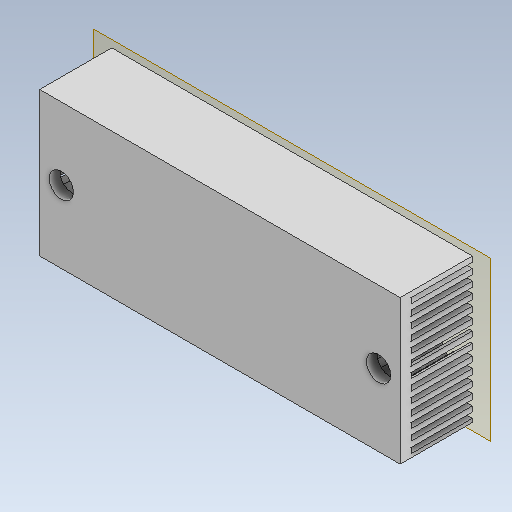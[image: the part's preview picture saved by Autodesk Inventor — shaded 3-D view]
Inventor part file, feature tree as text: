
AUTODESK INVENTOR PART (.ipt)
format: ipt  version: 2021 (Build 250183000, 183)  size: 220,160 bytes
history: native  units: in
note: dims shown in document units (in); Inventor stores cm internally (conversion verified against a paired STEP export)
features: other x3, sketch x3, plane x1
ambient origin geometry x8: Origin, YZ Plane, XZ Plane, XY Plane, X Axis, Y Axis, Z Axis, Center Point
bodies: Solid1 (feature_tree)
feature tree (7):
  other  "ExternalHeatSinkandClamp.ipt"
  other  "Solid1::ExternalHeatSinkandClamp.ipt"
  other  "TaggingFeature1"
  sketch  "Sketch1"  dims[d0=0.3937in]
  sketch  "Sketch2"  dims[d1=0.12in]
  sketch  "Sketch4"
  plane  "Work Plane1"
